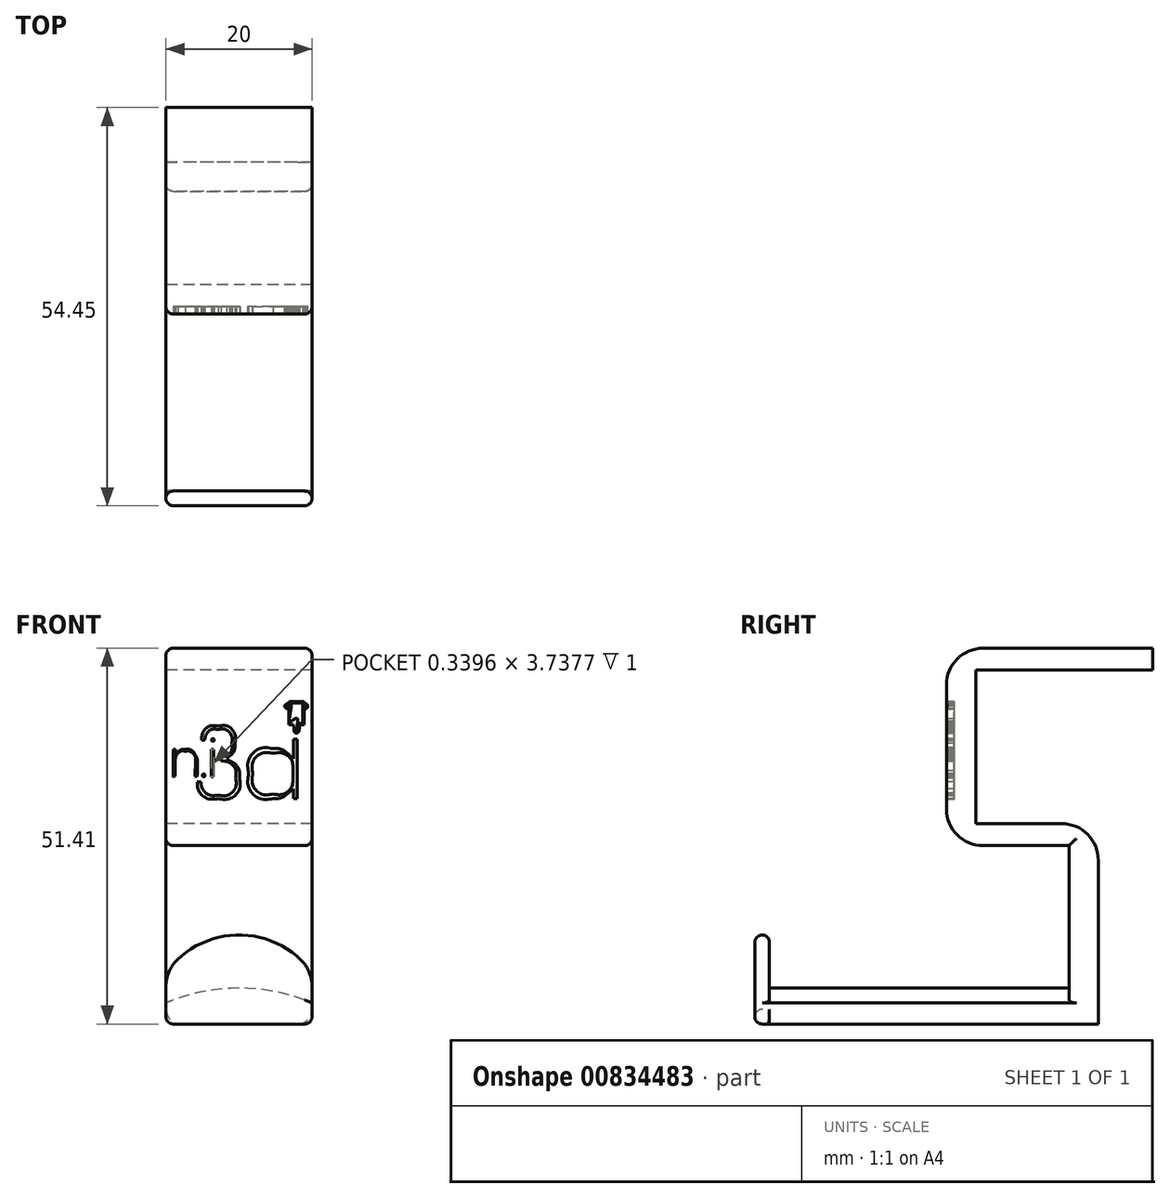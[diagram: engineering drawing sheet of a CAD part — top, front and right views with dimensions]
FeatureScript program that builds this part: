
annotation { "Feature Type Name" : "Feature", "Feature Type Description" : "" }
export const myFeature = defineFeature(function(context is Context, id is Id, definition is map)
    precondition{}
    {
        {
            var Q0;
            Q0=qCreatedBy(makeId("Right.planeOp"),FACE);
            var sketch = newSketch(context, id + "F0", { "sketchPlane" : qUnion([Q0])});
            skLineSegment(sketch, "E0", {"start": v(-10.53, 4.55) * mm, "end": v(13.69, 4.55) * mm});
            skLineSegment(sketch, "E1", {"start": v(13.69, 4.55) * mm, "end": v(13.69, 7.55) * mm});
            skLineSegment(sketch, "E2", {"start": v(13.69, 7.55) * mm, "end": v(-14.53, 7.55) * mm});
            skLineSegment(sketch, "E3", {"start": v(-14.53, 7.55) * mm, "end": v(-14.53, -19.45) * mm});
            skLineSegment(sketch, "E4", {"start": v(-14.53, -19.45) * mm, "end": v(2.24, -19.45) * mm});
            skLineSegment(sketch, "E5", {"start": v(2.24, -19.45) * mm, "end": v(2.24, -43.86) * mm});
            skLineSegment(sketch, "E6", {"start": v(2.24, -43.86) * mm, "end": v(6.24, -43.86) * mm});
            skLineSegment(sketch, "E7", {"start": v(6.24, -43.86) * mm, "end": v(6.24, -16.45) * mm});
            skLineSegment(sketch, "E8", {"start": v(6.24, -16.45) * mm, "end": v(-10.53, -16.45) * mm});
            skLineSegment(sketch, "E9", {"start": v(-10.53, -16.45) * mm, "end": v(-10.53, 4.55) * mm});
            skSolve(sketch);
        }
        {
            var Q0;
            Q0=makeQuery(id+"F0.imprint","IMPRINT",FACE,{"disambiguationData":[TD([[makeQuery(id+"F0.imprint","IMPRINT",EDGE,{"derivedFrom":sQuery(id+"F0.wireOp",EDGE,"E0")}),1.0]])]});
            extrude(context, id + "F1", {"entities" : qUnion([Q0]), "depth" : 20 * mm, "offsetDistance" : 25 * mm});
        }
        {
            var Q0;
            Q0=makeQuery(id+"F1.opExtrude","SWEPT_FACE",FACE,{"disambiguationData":[OSD([sQuery(id+"F0.wireOp",EDGE,"E7")])]});
            var sketch = newSketch(context, id + "F2", { "sketchPlane" : qUnion([Q0])});
            skLineSegment(sketch, "E10", {"start": v(-20, -43.86) * mm, "end": v(0, -43.86) * mm, "construction": true});
            skPoint(sketch, "E11", {"position": v(-10, -43.86) * mm});
            skArc(sketch, "E12", {"start": v(0, -40.98) * mm, "mid": v(-10, -38.94) * mm, "end": v(-20, -40.98) * mm});
            skLineSegment(sketch, "E13", {"start": v(0, -43.86) * mm, "end": v(-20, -43.86) * mm});
            skLineSegment(sketch, "E14", {"start": v(0, -40.98) * mm, "end": v(0, -43.86) * mm});
            skLineSegment(sketch, "E15", {"start": v(-20, -40.98) * mm, "end": v(-20, -43.86) * mm});
            skPoint(sketch, "E16.orphan", {"position": v(-25.08, -43.86) * mm});
            skPoint(sketch, "E17.orphan", {"position": v(5.08, -43.86) * mm});
            skSolve(sketch);
        }
        {
            var Q0;
            {var subQ0=sQuery(id+"F2.wireOp",EDGE,"E13");var subQ1=sQuery(id+"F2.wireOp",EDGE,"E12");var subQ2=makeQuery(id+"F2.imprint","INTERSECT",VERTEX,{"disambiguationData":[OD(1.0)],"derivedFrom":[subQ1,subQ0]});Q0=makeQuery(id+"F2.imprint","IMPRINT",FACE,{"disambiguationData":[TD([[makeQuery(id+"F2.imprint","IMPRINT",EDGE,{"disambiguationData":[TD([[subQ2,1.0]])],"derivedFrom":subQ1}),1.0]])]});}
            var Q1;
            {var subQ0=sQuery(id+"F2.wireOp",EDGE,"E13");var subQ1=sQuery(id+"F2.wireOp",EDGE,"E12");var subQ2=makeQuery(id+"F2.imprint","INTERSECT",VERTEX,{"disambiguationData":[OD(0.0)],"derivedFrom":[subQ1,subQ0]});Q1=makeQuery(id+"F2.imprint","IMPRINT",FACE,{"disambiguationData":[TD([[makeQuery(id+"F2.imprint","IMPRINT",EDGE,{"disambiguationData":[TD([[subQ2,-1.0]])],"derivedFrom":subQ1}),1.0]])]});}
            var Q2;
            {var subQ0=sQuery(id+"F2.wireOp",EDGE,"E12");var subQ1=sQuery(id+"F0.wireOp",EDGE,"E5");var subQ2=makeQuery(id+"F1.opExtrude","CAP_EDGE",EDGE,{"disambiguationData":[OSD([subQ1])],"isStart":false});var subQ3=makeQuery(id+"F2.imprint","INTERSECT",VERTEX,{"derivedFrom":[subQ2,subQ0]});Q2=makeQuery(id+"F2.imprint","IMPRINT",FACE,{"disambiguationData":[TD([[makeQuery(id+"F2.imprint","IMPRINT",EDGE,{"disambiguationData":[TD([[subQ3,-1.0]])],"derivedFrom":subQ0}),1.0]])]});}
            var Q3;
            {var subQ0=sQuery(id+"F2.wireOp",EDGE,"E12");var subQ1=sQuery(id+"F0.wireOp",EDGE,"E7");var subQ2=makeQuery(id+"F1.opExtrude","CAP_EDGE",EDGE,{"disambiguationData":[OSD([subQ1])],"isStart":true});var subQ3=makeQuery(id+"F2.imprint","INTERSECT",VERTEX,{"derivedFrom":[subQ2,subQ0]});Q3=makeQuery(id+"F2.imprint","IMPRINT",FACE,{"disambiguationData":[TD([[makeQuery(id+"F2.imprint","IMPRINT",EDGE,{"disambiguationData":[TD([[subQ3,-1.0]])],"derivedFrom":subQ0}),1.0]])]});}
            extrude(context, id + "F3", {"entities" : qUnion([Q0, Q1, Q2, Q3]), "operationType" : NewBodyOperationType.ADD, "oppositeDirection" : true, "depth" : 45 * mm, "offsetDistance" : 25 * mm});
        }
        {
            var Q0;
            {var subQ0=sQuery(id+"F2.wireOp",EDGE,"E13");var subQ1=sQuery(id+"F2.wireOp",EDGE,"E12");Q0=makeQuery(id+"F3.opExtrude","SWEPT_EDGE",EDGE,{"disambiguationData":[OSD([subQ1,subQ0]),TDD([makeQuery(id+"F2.imprint","INTERSECT",VERTEX,{"disambiguationData":[OD(0.0)],"derivedFrom":[subQ1,subQ0]})])]});}
            var Q1;
            {var subQ0=sQuery(id+"F2.wireOp",EDGE,"E13");var subQ1=sQuery(id+"F2.wireOp",EDGE,"E12");Q1=makeQuery(id+"F3.opExtrude","SWEPT_EDGE",EDGE,{"disambiguationData":[OSD([subQ1,subQ0]),TDD([makeQuery(id+"F2.imprint","INTERSECT",VERTEX,{"disambiguationData":[OD(1.0)],"derivedFrom":[subQ1,subQ0]})])]});}
            fillet(context, id + "F4", {"entities" : qUnion([Q0, Q1]), "tangentPropagation" : true, "radius" : 2 * mm, "defaultsChanged" : true, "vertexSettings" : [], "allowEdgeOverflow" : false});
        }
        {
            var Q0;
            Q0=makeQuery(id+"F1.opExtrude","SWEPT_EDGE",EDGE,{"disambiguationData":[OSD([sQuery(id+"F0.wireOp",EDGE,"E2"),sQuery(id+"F0.wireOp",EDGE,"E3")])]});
            var Q1;
            Q1=makeQuery(id+"F1.opExtrude","SWEPT_EDGE",EDGE,{"disambiguationData":[OSD([sQuery(id+"F0.wireOp",EDGE,"E3"),sQuery(id+"F0.wireOp",EDGE,"E4")])]});
            fillet(context, id + "F5", {"entities" : qUnion([Q0, Q1]), "tangentPropagation" : true, "radius" : 5 * mm, "defaultsChanged" : false, "vertexSettings" : [], "allowEdgeOverflow" : false});
        }
        {
            var Q0;
            Q0=makeQuery(id+"F1.opExtrude","SWEPT_EDGE",EDGE,{"disambiguationData":[OSD([sQuery(id+"F0.wireOp",EDGE,"E7"),sQuery(id+"F0.wireOp",EDGE,"E8")])]});
            fillet(context, id + "F6", {"entities" : qUnion([Q0]), "tangentPropagation" : true, "radius" : 5 * mm, "defaultsChanged" : false, "vertexSettings" : [], "allowEdgeOverflow" : false});
        }
        {
            var Q0;
            Q0=makeQuery(id+"F3.opExtrude","CAP_FACE",FACE,{"disambiguationData":[OSD([sQuery(id+"F2.wireOp",EDGE,"E12"),sQuery(id+"F2.wireOp",EDGE,"E13")])],"isStart":false});
            var sketch = newSketch(context, id + "F7", { "sketchPlane" : qUnion([Q0])});
            skArc(sketch, "E18", {"start": v(0, -36.9) * mm, "mid": v(10, -31.68) * mm, "end": v(20, -36.9) * mm});
            skPoint(sketch, "E18.startSnap0", {"position": v(10, -43.86) * mm});
            skLineSegment(sketch, "E19", {"start": v(0, -43.86) * mm, "end": v(20, -43.86) * mm});
            skLineSegment(sketch, "E20", {"start": v(20, -36.9) * mm, "end": v(20, -43.86) * mm});
            skLineSegment(sketch, "E21", {"start": v(0, -36.9) * mm, "end": v(0, -43.86) * mm});
            skSolve(sketch);
        }
        {
            var Q0;
            Q0 = qSketchRegion(id + "F7", true);
            extrude(context, id + "F8", {"entities" : qUnion([Q0]), "operationType" : NewBodyOperationType.ADD, "depth" : 2 * mm, "offsetDistance" : 25 * mm});
        }
        {
            var Q0;
            Q0=makeQuery(id+"F1.opExtrude","SWEPT_FACE",FACE,{"disambiguationData":[OSD([sQuery(id+"F0.wireOp",EDGE,"E3")])]});
            var sketch = newSketch(context, id + "F9", { "sketchPlane" : qUnion([Q0])});
            skLineSegment(sketch, "E22", {"start": v(4.02, -7.84) * mm, "end": v(4, -10) * mm});
            skLineSegment(sketch, "E23", {"start": v(4, -10) * mm, "end": v(4.27, -10) * mm});
            skLineSegment(sketch, "E24", {"start": v(1.3, -7.04) * mm, "end": v(1.3, -6.28) * mm});
            skLineSegment(sketch, "E25", {"start": v(1.3, -6.28) * mm, "end": v(1.02, -6.27) * mm});
            skLineSegment(sketch, "E26", {"start": v(1.02, -6.27) * mm, "end": v(0.98, -9.98) * mm});
            skLineSegment(sketch, "E27", {"start": v(0.98, -9.98) * mm, "end": v(1.26, -9.98) * mm});
            skLineSegment(sketch, "E28", {"start": v(1.26, -9.98) * mm, "end": v(1.28, -7.62) * mm});
            skLineSegment(sketch, "E29", {"start": v(6.24, -6.32) * mm, "end": v(6.2, -10.05) * mm});
            skLineSegment(sketch, "E30", {"start": v(6.2, -10.05) * mm, "end": v(6.5, -10.06) * mm});
            skLineSegment(sketch, "E31", {"start": v(6.5, -10.06) * mm, "end": v(6.54, -6.32) * mm});
            skLineSegment(sketch, "E32", {"start": v(6.54, -6.32) * mm, "end": v(6.24, -6.32) * mm});
            skLineSegment(sketch, "E33", {"start": v(8.78, -7.86) * mm, "end": v(8.34, -7.56) * mm});
            skLineSegment(sketch, "E34", {"start": v(8.34, -7.56) * mm, "end": v(8.72, -7.2) * mm});
            skLineSegment(sketch, "E35", {"start": v(4.88, -5.05) * mm, "end": v(5.33, -5.05) * mm});
            skLineSegment(sketch, "E36", {"start": v(7.56, -7.32) * mm, "end": v(7.56, -7.89) * mm});
            skLineSegment(sketch, "E37", {"start": v(4.8, -10.71) * mm, "end": v(4.27, -10.71) * mm});
            skLineSegment(sketch, "E38", {"start": v(16.72, -12.25) * mm, "end": v(17.43, -11.66) * mm});
            skLineSegment(sketch, "E39", {"start": v(17.43, -11.66) * mm, "end": v(17.43, -13.01) * mm});
            skLineSegment(sketch, "E40", {"start": v(17.43, -13.01) * mm, "end": v(17.98, -13.01) * mm});
            skLineSegment(sketch, "E41", {"start": v(17.98, -13.01) * mm, "end": v(17.98, -4.92) * mm});
            skLineSegment(sketch, "E42", {"start": v(17.98, -4.92) * mm, "end": v(17.43, -4.92) * mm});
            skLineSegment(sketch, "E43", {"start": v(17.43, -4.92) * mm, "end": v(17.43, -7.54) * mm});
            skLineSegment(sketch, "E44", {"start": v(17.43, -7.54) * mm, "end": v(16.72, -6.94) * mm});
            skLineSegment(sketch, "E45", {"start": v(17.38, -9.23) * mm, "end": v(17.38, -9.96) * mm});
            skLineSegment(sketch, "E46", {"start": v(17.5, -3.3) * mm, "end": v(17.47, -2.93) * mm});
            skLineSegment(sketch, "E47", {"start": v(17.47, -2.93) * mm, "end": v(17.16, -2.92) * mm});
            skLineSegment(sketch, "E48", {"start": v(17.16, -2.92) * mm, "end": v(16.84, -2.9) * mm});
            skLineSegment(sketch, "E49", {"start": v(16.84, -2.9) * mm, "end": v(16.83, -1.34) * mm});
            skLineSegment(sketch, "E50", {"start": v(16.83, -1.34) * mm, "end": v(16.82, 0.23) * mm});
            skLineSegment(sketch, "E51", {"start": v(16.82, 0.23) * mm, "end": v(17.88, 0.23) * mm});
            skLineSegment(sketch, "E52", {"start": v(17.88, 0.23) * mm, "end": v(18.94, 0.23) * mm});
            skLineSegment(sketch, "E53", {"start": v(18.94, 0.23) * mm, "end": v(18.93, -1.34) * mm});
            skLineSegment(sketch, "E54", {"start": v(18.93, -1.34) * mm, "end": v(18.92, -2.9) * mm});
            skLineSegment(sketch, "E55", {"start": v(18.92, -2.9) * mm, "end": v(18.6, -2.92) * mm});
            skLineSegment(sketch, "E56", {"start": v(18.6, -2.92) * mm, "end": v(18.3, -2.93) * mm});
            skLineSegment(sketch, "E57", {"start": v(18.3, -2.93) * mm, "end": v(18.27, -3.27) * mm});
            skLineSegment(sketch, "E58", {"start": v(18.08, -3.19) * mm, "end": v(18.1, -2.74) * mm});
            skLineSegment(sketch, "E59", {"start": v(18.1, -2.74) * mm, "end": v(18.43, -2.74) * mm});
            skLineSegment(sketch, "E60", {"start": v(18.43, -2.74) * mm, "end": v(18.75, -2.74) * mm});
            skLineSegment(sketch, "E61", {"start": v(18.75, -2.74) * mm, "end": v(18.75, -1.35) * mm});
            skLineSegment(sketch, "E62", {"start": v(18.75, -1.35) * mm, "end": v(18.75, 0.04) * mm});
            skLineSegment(sketch, "E63", {"start": v(18.75, 0.04) * mm, "end": v(18.33, 0.04) * mm});
            skLineSegment(sketch, "E64", {"start": v(18.33, 0.04) * mm, "end": v(17.91, 0.04) * mm});
            skLineSegment(sketch, "E65", {"start": v(17.91, 0.04) * mm, "end": v(17.05, 0.02) * mm});
            skFitSpline(sketch, "E66", {"points": [v(2.67, -6.55) * mm, v(3.3, -6.55) * mm, v(3.97, -7.17) * mm, v(4.02, -7.84) * mm]});
            skFitSpline(sketch, "E67", {"points": [v(4.27, -10) * mm, v(4.31, -8.36) * mm, v(4.3, -8.07) * mm, v(4.3, -7.94) * mm]});
            skFitSpline(sketch, "E68", {"points": [v(4.3, -7.94) * mm, v(4.28, -7.66) * mm, v(4.2, -7.38) * mm, v(4.06, -7.14) * mm]});
            skFitSpline(sketch, "E69", {"points": [v(4.06, -7.14) * mm, v(3.76, -6.6) * mm, v(3.24, -6.28) * mm, v(2.67, -6.28) * mm]});
            skFitSpline(sketch, "E70", {"points": [v(2.67, -6.28) * mm, v(2.31, -6.27) * mm, v(1.96, -6.4) * mm, v(1.67, -6.63) * mm]});
            skFitSpline(sketch, "E71", {"points": [v(1.67, -6.63) * mm, v(1.49, -6.77) * mm, v(1.3, -7.02) * mm, v(1.3, -7.04) * mm, v(1.3, -7.04) * mm, v(1.3, -7.04) * mm]});
            skFitSpline(sketch, "E72", {"points": [v(1.28, -7.62) * mm, v(1.47, -6.99) * mm, v(2.04, -6.54) * mm, v(2.67, -6.55) * mm]});
            skFitSpline(sketch, "E73", {"points": [v(5.18, -9.68) * mm, v(5.1, -9.68) * mm, v(5.02, -9.76) * mm, v(5.02, -9.85) * mm]});
            skFitSpline(sketch, "E74", {"points": [v(5.02, -9.85) * mm, v(5.02, -9.94) * mm, v(5.1, -10) * mm, v(5.18, -10.01) * mm]});
            skFitSpline(sketch, "E75", {"points": [v(5.18, -10.01) * mm, v(5.28, -10.01) * mm, v(5.34, -9.95) * mm, v(5.35, -9.85) * mm]});
            skFitSpline(sketch, "E76", {"points": [v(5.35, -9.85) * mm, v(5.35, -9.76) * mm, v(5.28, -9.68) * mm, v(5.18, -9.68) * mm]});
            skFitSpline(sketch, "E77", {"points": [v(6.42, -5.17) * mm, v(6.52, -5.18) * mm, v(6.6, -5.1) * mm, v(6.6, -5.01) * mm]});
            skFitSpline(sketch, "E78", {"points": [v(6.6, -5.01) * mm, v(6.6, -4.92) * mm, v(6.52, -4.84) * mm, v(6.43, -4.84) * mm]});
            skFitSpline(sketch, "E79", {"points": [v(6.43, -4.84) * mm, v(6.34, -4.84) * mm, v(6.26, -4.91) * mm, v(6.25, -5) * mm]});
            skFitSpline(sketch, "E80", {"points": [v(6.25, -5) * mm, v(6.25, -5.1) * mm, v(6.33, -5.17) * mm, v(6.42, -5.17) * mm]});
            skFitSpline(sketch, "E81", {"points": [v(7.14, -13.03) * mm, v(8.75, -13.03) * mm, v(10.06, -11.76) * mm, v(10.06, -10.2) * mm]});
            skFitSpline(sketch, "E82", {"points": [v(10.06, -10.2) * mm, v(10.06, -9.26) * mm, v(9.58, -8.4) * mm, v(8.78, -7.86) * mm]});
            skFitSpline(sketch, "E83", {"points": [v(8.72, -7.2) * mm, v(9.19, -6.75) * mm, v(9.44, -6.14) * mm, v(9.44, -5.48) * mm]});
            skFitSpline(sketch, "E84", {"points": [v(9.44, -5.48) * mm, v(9.44, -4.16) * mm, v(8.4, -3.1) * mm, v(7.14, -3.1) * mm]});
            skFitSpline(sketch, "E85", {"points": [v(7.14, -3.1) * mm, v(6, -3.1) * mm, v(5.06, -3.95) * mm, v(4.88, -5.05) * mm]});
            skFitSpline(sketch, "E86", {"points": [v(5.33, -5.05) * mm, v(5.52, -4.2) * mm, v(6.26, -3.57) * mm, v(7.14, -3.57) * mm]});
            skFitSpline(sketch, "E87", {"points": [v(7.14, -3.57) * mm, v(8.17, -3.57) * mm, v(9, -4.43) * mm, v(9, -5.48) * mm]});
            skFitSpline(sketch, "E88", {"points": [v(9, -5.48) * mm, v(9, -6.38) * mm, v(8.4, -7.13) * mm, v(7.56, -7.32) * mm]});
            skFitSpline(sketch, "E89", {"points": [v(7.56, -7.89) * mm, v(8.7, -8.09) * mm, v(9.54, -9.05) * mm, v(9.54, -10.2) * mm]});
            skFitSpline(sketch, "E90", {"points": [v(9.54, -10.2) * mm, v(9.54, -11.49) * mm, v(8.47, -12.55) * mm, v(7.14, -12.55) * mm]});
            skFitSpline(sketch, "E91", {"points": [v(7.14, -12.55) * mm, v(6, -12.55) * mm, v(5.04, -11.77) * mm, v(4.8, -10.71) * mm]});
            skFitSpline(sketch, "E92", {"points": [v(4.27, -10.71) * mm, v(4.53, -12.03) * mm, v(5.73, -13.03) * mm, v(7.14, -13.03) * mm]});
            skFitSpline(sketch, "E93", {"points": [v(14.63, -6.18) * mm, v(12.81, -6.18) * mm, v(11.31, -7.72) * mm, v(11.31, -9.6) * mm]});
            skFitSpline(sketch, "E94", {"points": [v(11.31, -9.6) * mm, v(11.31, -11.47) * mm, v(12.81, -13.01) * mm, v(14.63, -13.01) * mm]});
            skFitSpline(sketch, "E95", {"points": [v(14.63, -13.01) * mm, v(15.4, -13.01) * mm, v(16.11, -12.75) * mm, v(16.72, -12.25) * mm]});
            skFitSpline(sketch, "E96", {"points": [v(16.72, -6.94) * mm, v(16.11, -6.45) * mm, v(15.4, -6.18) * mm, v(14.63, -6.18) * mm]});
            skFitSpline(sketch, "E97", {"points": [v(14.63, -12.4) * mm, v(13.08, -12.4) * mm, v(11.9, -11.18) * mm, v(11.9, -9.6) * mm]});
            skFitSpline(sketch, "E98", {"points": [v(11.9, -9.6) * mm, v(11.9, -8.02) * mm, v(13.08, -6.83) * mm, v(14.63, -6.83) * mm]});
            skFitSpline(sketch, "E99", {"points": [v(14.63, -6.83) * mm, v(16.04, -6.83) * mm, v(17.2, -7.8) * mm, v(17.38, -9.23) * mm]});
            skFitSpline(sketch, "E100", {"points": [v(17.38, -9.96) * mm, v(17.2, -11.4) * mm, v(16.04, -12.4) * mm, v(14.63, -12.4) * mm]});
            skFitSpline(sketch, "E101", {"points": [v(17.7, -4.01) * mm, v(17.58, -3.89) * mm, v(17.52, -3.68) * mm, v(17.5, -3.3) * mm]});
            skFitSpline(sketch, "E102", {"points": [v(18.27, -3.27) * mm, v(18.24, -3.68) * mm, v(18.2, -3.83) * mm, v(18.05, -4.02) * mm]});
            skFitSpline(sketch, "E103", {"points": [v(18.05, -4.02) * mm, v(17.98, -4.04) * mm, v(17.78, -4.06) * mm, v(17.7, -4.01) * mm]});
            skFitSpline(sketch, "E104", {"points": [v(18, -3.77) * mm, v(18.03, -3.69) * mm, v(18.06, -3.47) * mm, v(18.08, -3.19) * mm]});
            skFitSpline(sketch, "E105", {"points": [v(17.05, 0.02) * mm, v(17.13, -0.43) * mm, v(16.92, -2.55) * mm, v(17.24, -2.41) * mm]});
            skFitSpline(sketch, "E106", {"points": [v(17.24, -2.41) * mm, v(17.98, -2.09) * mm, v(17.86, -3.93) * mm, v(17.9, -3.91) * mm]});
            skFitSpline(sketch, "E107", {"points": [v(17.9, -3.91) * mm, v(17.91, -3.9) * mm, v(17.96, -3.84) * mm, v(18, -3.77) * mm]});
            skFitSpline(sketch, "E108", {"points": [v(16.42, -0.63) * mm, v(16.29, -0.5) * mm, v(16.28, -0.27) * mm, v(16.42, -0.14) * mm]});
            skFitSpline(sketch, "E109", {"points": [v(16.42, -0.14) * mm, v(16.47, -0.08) * mm, v(16.55, -0.04) * mm, v(16.6, -0.04) * mm]});
            skFitSpline(sketch, "E110", {"points": [v(16.6, -0.04) * mm, v(16.66, -0.04) * mm, v(16.67, -0.07) * mm, v(16.67, -0.39) * mm]});
            skFitSpline(sketch, "E111", {"points": [v(16.67, -0.39) * mm, v(16.67, -0.7) * mm, v(16.66, -0.73) * mm, v(16.6, -0.73) * mm]});
            skFitSpline(sketch, "E112", {"points": [v(16.6, -0.73) * mm, v(16.56, -0.73) * mm, v(16.48, -0.69) * mm, v(16.42, -0.63) * mm]});
            skFitSpline(sketch, "E113", {"points": [v(19.02, -0.39) * mm, v(19.02, -0.08) * mm, v(19.02, -0.04) * mm, v(19.09, -0.04) * mm]});
            skFitSpline(sketch, "E114", {"points": [v(19.09, -0.04) * mm, v(19.2, -0.04) * mm, v(19.35, -0.18) * mm, v(19.37, -0.3) * mm]});
            skFitSpline(sketch, "E115", {"points": [v(19.37, -0.3) * mm, v(19.4, -0.44) * mm, v(19.34, -0.6) * mm, v(19.23, -0.67) * mm]});
            skFitSpline(sketch, "E116", {"points": [v(19.23, -0.67) * mm, v(19.04, -0.8) * mm, v(19.02, -0.77) * mm, v(19.02, -0.39) * mm]});
            skFitSpline(sketch, "E117", {"points": [v(17.3, -5.04) * mm, v(17.15, -4.77) * mm, v(17.22, -4.57) * mm, v(17.52, -4.33) * mm]});
            skFitSpline(sketch, "E118", {"points": [v(17.52, -4.33) * mm, v(17.75, -4.14) * mm, v(17.8, -4.07) * mm, v(17.73, -4) * mm]});
            skFitSpline(sketch, "E119", {"points": [v(17.73, -4) * mm, v(17.98, -4) * mm, v(18.01, -4) * mm, v(18.02, -4) * mm, v(18.02, -4) * mm, v(18.02, -4) * mm]});
            skFitSpline(sketch, "E120", {"points": [v(18.02, -4) * mm, v(17.97, -4.07) * mm, v(17.93, -4.15) * mm, v(17.93, -4.17) * mm]});
            skFitSpline(sketch, "E121", {"points": [v(17.93, -4.17) * mm, v(17.93, -4.19) * mm, v(17.86, -4.26) * mm, v(17.78, -4.34) * mm]});
            skFitSpline(sketch, "E122", {"points": [v(17.78, -4.34) * mm, v(17.38, -4.72) * mm, v(17.4, -4.7) * mm, v(17.41, -4.83) * mm]});
            skFitSpline(sketch, "E123", {"points": [v(17.41, -4.83) * mm, v(17.45, -4.9) * mm, v(17.35, -5.1) * mm, v(17.3, -5.04) * mm]});
            skSolve(sketch);
        }
        {
            var Q0;
            Q0 = qSketchRegion(id + "F9", true);
            extrude(context, id + "F10", {"entities" : qUnion([Q0]), "operationType" : NewBodyOperationType.REMOVE, "oppositeDirection" : true, "depth" : 1 * mm, "offsetDistance" : 25 * mm});
        }
        {
            var Q0;
            Q0=makeQuery(id+"F8.opExtrude","SWEPT_EDGE",EDGE,{"disambiguationData":[OSD([sQuery(id+"F7.wireOp",EDGE,"E19"),sQuery(id+"F7.wireOp",EDGE,"E20")])]});
            var Q1;
            Q1=makeQuery(id+"F8.opExtrude","SWEPT_EDGE",EDGE,{"disambiguationData":[OSD([sQuery(id+"F7.wireOp",EDGE,"E19"),sQuery(id+"F7.wireOp",EDGE,"E21")])]});
            fillet(context, id + "F11", {"entities" : qUnion([Q0, Q1]), "tangentPropagation" : true, "radius" : 1 * mm, "defaultsChanged" : true, "vertexSettings" : [], "allowEdgeOverflow" : false});
        }
        {
            var Q0;
            Q0=makeQuery(id+"F8.opExtrude","SWEPT_EDGE",EDGE,{"disambiguationData":[OSD([sQuery(id+"F7.wireOp",EDGE,"E18"),sQuery(id+"F7.wireOp",EDGE,"E21")])]});
            var Q1;
            Q1=makeQuery(id+"F8.opExtrude","SWEPT_EDGE",EDGE,{"disambiguationData":[OSD([sQuery(id+"F7.wireOp",EDGE,"E18"),sQuery(id+"F7.wireOp",EDGE,"E20")])]});
            fillet(context, id + "F12", {"entities" : qUnion([Q0, Q1]), "tangentPropagation" : true, "radius" : 5 * mm, "defaultsChanged" : false, "vertexSettings" : [], "allowEdgeOverflow" : false});
        }
        {
            var Q0;
            Q0=makeQuery(id+"F8.opExtrude","CAP_EDGE",EDGE,{"disambiguationData":[OSD([sQuery(id+"F7.wireOp",EDGE,"E18")])],"isStart":true});
            var Q1;
            Q1=makeQuery(id+"F8.opExtrude","CAP_EDGE",EDGE,{"disambiguationData":[OSD([sQuery(id+"F7.wireOp",EDGE,"E18")])],"isStart":false});
            var Q2;
            {var subQ0=sQuery(id+"F7.wireOp",EDGE,"E21");var subQ1=sQuery(id+"F7.wireOp",EDGE,"E18");Q2=makeQuery(id+"F12.opFillet","BLEND_EDGE",EDGE,{"blendedFrom":[makeQuery(id+"F8.opExtrude","SWEPT_EDGE",EDGE,{"disambiguationData":[OSD([subQ1,subQ0])]}),makeQuery(id+"F8.opExtrude","CAP_FACE",FACE,{"disambiguationData":[OSD([subQ1,sQuery(id+"F7.wireOp",EDGE,"E19"),sQuery(id+"F7.wireOp",EDGE,"E20"),subQ0])],"isStart":false})],"blendedInto":[makeQuery(id+"F8.opExtrude","CAP_FACE",FACE,{"disambiguationData":[OSD([subQ1,sQuery(id+"F7.wireOp",EDGE,"E19"),sQuery(id+"F7.wireOp",EDGE,"E20"),subQ0])],"isStart":false})]});}
            var Q3;
            {var subQ0=sQuery(id+"F7.wireOp",EDGE,"E21");var subQ11=sQuery(id+"F7.wireOp",EDGE,"E18");var subQ12=sQuery(id+"F7.wireOp",EDGE,"E20");Q3=makeQuery(id+"F12.opFillet","BLEND_EDGE",EDGE,{"blendedFrom":[makeQuery(id+"F8.opExtrude","SWEPT_EDGE",EDGE,{"disambiguationData":[OSD([subQ11,subQ0])]}),makeQuery(id+"F8.boolean.opBoolean","SPLIT",FACE,{"disambiguationData":[TD([makeQuery(id+"F3.opExtrude","SWEPT_FACE",FACE,{"disambiguationData":[OSD([sQuery(id+"F2.wireOp",EDGE,"E12")])]})])],"derivedFrom":makeQuery(id+"F8.opExtrude","CAP_FACE",FACE,{"disambiguationData":[OSD([subQ11,sQuery(id+"F7.wireOp",EDGE,"E19"),subQ12,subQ0])],"isStart":true})})],"blendedInto":[makeQuery(id+"F8.boolean.opBoolean","SPLIT",FACE,{"disambiguationData":[TD([makeQuery(id+"F3.opExtrude","SWEPT_FACE",FACE,{"disambiguationData":[OSD([sQuery(id+"F2.wireOp",EDGE,"E12")])]})])],"derivedFrom":makeQuery(id+"F8.opExtrude","CAP_FACE",FACE,{"disambiguationData":[OSD([subQ11,sQuery(id+"F7.wireOp",EDGE,"E19"),subQ12,subQ0])],"isStart":true})})]});}
            var Q4;
            {var subQ0=sQuery(id+"F7.wireOp",EDGE,"E21");Q4=makeQuery(id+"F8.boolean.opBoolean","SPLIT",EDGE,{"disambiguationData":[TD([makeQuery(id+"F3.opExtrude","SWEPT_FACE",FACE,{"disambiguationData":[OSD([sQuery(id+"F2.wireOp",EDGE,"E12")])]})])],"derivedFrom":makeQuery(id+"F8.opExtrude","CAP_EDGE",EDGE,{"disambiguationData":[OSD([subQ0])],"isStart":true})});}
            var Q5;
            Q5=makeQuery(id+"F8.opExtrude","CAP_EDGE",EDGE,{"disambiguationData":[OSD([sQuery(id+"F7.wireOp",EDGE,"E21")])],"isStart":false});
            var Q6;
            {var subQ0=sQuery(id+"F7.wireOp",EDGE,"E20");var subQ1=sQuery(id+"F7.wireOp",EDGE,"E18");Q6=makeQuery(id+"F12.opFillet","BLEND_EDGE",EDGE,{"blendedFrom":[makeQuery(id+"F8.opExtrude","SWEPT_EDGE",EDGE,{"disambiguationData":[OSD([subQ1,subQ0])]}),makeQuery(id+"F8.opExtrude","CAP_FACE",FACE,{"disambiguationData":[OSD([subQ1,sQuery(id+"F7.wireOp",EDGE,"E19"),subQ0,sQuery(id+"F7.wireOp",EDGE,"E21")])],"isStart":false})],"blendedInto":[makeQuery(id+"F8.opExtrude","CAP_FACE",FACE,{"disambiguationData":[OSD([subQ1,sQuery(id+"F7.wireOp",EDGE,"E19"),subQ0,sQuery(id+"F7.wireOp",EDGE,"E21")])],"isStart":false})]});}
            var Q7;
            Q7=makeQuery(id+"F8.opExtrude","CAP_EDGE",EDGE,{"disambiguationData":[OSD([sQuery(id+"F7.wireOp",EDGE,"E20")])],"isStart":false});
            var Q8;
            {var subQ0=sQuery(id+"F7.wireOp",EDGE,"E21");var subQ1=sQuery(id+"F7.wireOp",EDGE,"E19");Q8=makeQuery(id+"F11.opFillet","BLEND_EDGE",EDGE,{"blendedFrom":[makeQuery(id+"F8.opExtrude","SWEPT_EDGE",EDGE,{"disambiguationData":[OSD([subQ1,subQ0])]}),makeQuery(id+"F8.opExtrude","CAP_FACE",FACE,{"disambiguationData":[OSD([sQuery(id+"F7.wireOp",EDGE,"E18"),subQ1,sQuery(id+"F7.wireOp",EDGE,"E20"),subQ0])],"isStart":false})],"blendedInto":[makeQuery(id+"F8.opExtrude","CAP_FACE",FACE,{"disambiguationData":[OSD([sQuery(id+"F7.wireOp",EDGE,"E18"),subQ1,sQuery(id+"F7.wireOp",EDGE,"E20"),subQ0])],"isStart":false})]});}
            var Q9;
            Q9=makeQuery(id+"F8.opExtrude","CAP_EDGE",EDGE,{"disambiguationData":[OSD([sQuery(id+"F7.wireOp",EDGE,"E19")])],"isStart":false});
            var Q10;
            {var subQ0=sQuery(id+"F7.wireOp",EDGE,"E20");var subQ1=sQuery(id+"F7.wireOp",EDGE,"E19");Q10=makeQuery(id+"F11.opFillet","BLEND_EDGE",EDGE,{"blendedFrom":[makeQuery(id+"F8.opExtrude","SWEPT_EDGE",EDGE,{"disambiguationData":[OSD([subQ1,subQ0])]}),makeQuery(id+"F8.opExtrude","CAP_FACE",FACE,{"disambiguationData":[OSD([sQuery(id+"F7.wireOp",EDGE,"E18"),subQ1,subQ0,sQuery(id+"F7.wireOp",EDGE,"E21")])],"isStart":false})],"blendedInto":[makeQuery(id+"F8.opExtrude","CAP_FACE",FACE,{"disambiguationData":[OSD([sQuery(id+"F7.wireOp",EDGE,"E18"),subQ1,subQ0,sQuery(id+"F7.wireOp",EDGE,"E21")])],"isStart":false})]});}
            var Q11;
            {var subQ0=sQuery(id+"F7.wireOp",EDGE,"E21");var subQ11=sQuery(id+"F7.wireOp",EDGE,"E18");var subQ12=sQuery(id+"F7.wireOp",EDGE,"E20");Q11=makeQuery(id+"F12.opFillet","BLEND_EDGE",EDGE,{"blendedFrom":[makeQuery(id+"F8.opExtrude","SWEPT_EDGE",EDGE,{"disambiguationData":[OSD([subQ11,subQ12])]}),makeQuery(id+"F8.boolean.opBoolean","SPLIT",FACE,{"disambiguationData":[TD([makeQuery(id+"F3.opExtrude","SWEPT_FACE",FACE,{"disambiguationData":[OSD([sQuery(id+"F2.wireOp",EDGE,"E12")])]})])],"derivedFrom":makeQuery(id+"F8.opExtrude","CAP_FACE",FACE,{"disambiguationData":[OSD([subQ11,sQuery(id+"F7.wireOp",EDGE,"E19"),subQ12,subQ0])],"isStart":true})})],"blendedInto":[makeQuery(id+"F8.boolean.opBoolean","SPLIT",FACE,{"disambiguationData":[TD([makeQuery(id+"F3.opExtrude","SWEPT_FACE",FACE,{"disambiguationData":[OSD([sQuery(id+"F2.wireOp",EDGE,"E12")])]})])],"derivedFrom":makeQuery(id+"F8.opExtrude","CAP_FACE",FACE,{"disambiguationData":[OSD([subQ11,sQuery(id+"F7.wireOp",EDGE,"E19"),subQ12,subQ0])],"isStart":true})})]});}
            var Q12;
            {var subQ1=sQuery(id+"F7.wireOp",EDGE,"E20");Q12=makeQuery(id+"F8.boolean.opBoolean","SPLIT",EDGE,{"disambiguationData":[TD([makeQuery(id+"F3.opExtrude","SWEPT_FACE",FACE,{"disambiguationData":[OSD([sQuery(id+"F2.wireOp",EDGE,"E12")])]})])],"derivedFrom":makeQuery(id+"F8.opExtrude","CAP_EDGE",EDGE,{"disambiguationData":[OSD([subQ1])],"isStart":true})});}
            fillet(context, id + "F13", {"entities" : qUnion([Q0, Q1, Q2, Q3, Q4, Q5, Q6, Q7, Q8, Q9, Q10, Q11, Q12]), "tangentPropagation" : true, "radius" : 1 * mm, "defaultsChanged" : true, "vertexSettings" : [], "allowEdgeOverflow" : false});
        }
        {
            var Q0;
            Q0=makeQuery(id+"F1.opExtrude","CAP_EDGE",EDGE,{"disambiguationData":[OSD([sQuery(id+"F0.wireOp",EDGE,"E3")])],"isStart":true});
            var Q1;
            {var subQ0=sQuery(id+"F0.wireOp",EDGE,"E3");var subQ1=sQuery(id+"F0.wireOp",EDGE,"E2");Q1=makeQuery(id+"F5.opFillet","BLEND_EDGE",EDGE,{"blendedFrom":[makeQuery(id+"F1.opExtrude","SWEPT_EDGE",EDGE,{"disambiguationData":[OSD([subQ1,subQ0])]}),makeQuery(id+"F3.boolean.opBoolean","MERGE",FACE,{"derivedFrom":[makeQuery(id+"F1.opExtrude","CAP_FACE",FACE,{"disambiguationData":[OSD([sQuery(id+"F0.wireOp",EDGE,"E0"),sQuery(id+"F0.wireOp",EDGE,"E1"),subQ1,subQ0,sQuery(id+"F0.wireOp",EDGE,"E4"),sQuery(id+"F0.wireOp",EDGE,"E5"),sQuery(id+"F0.wireOp",EDGE,"E6"),sQuery(id+"F0.wireOp",EDGE,"E7"),sQuery(id+"F0.wireOp",EDGE,"E8"),sQuery(id+"F0.wireOp",EDGE,"E9")])],"isStart":true}),makeQuery(id+"F3.opExtrude","SWEPT_FACE",FACE,{"disambiguationData":[OSD([sQuery(id+"F2.wireOp",EDGE,"E14")])]})]})],"blendedInto":[makeQuery(id+"F3.boolean.opBoolean","MERGE",FACE,{"derivedFrom":[makeQuery(id+"F1.opExtrude","CAP_FACE",FACE,{"disambiguationData":[OSD([sQuery(id+"F0.wireOp",EDGE,"E0"),sQuery(id+"F0.wireOp",EDGE,"E1"),subQ1,subQ0,sQuery(id+"F0.wireOp",EDGE,"E4"),sQuery(id+"F0.wireOp",EDGE,"E5"),sQuery(id+"F0.wireOp",EDGE,"E6"),sQuery(id+"F0.wireOp",EDGE,"E7"),sQuery(id+"F0.wireOp",EDGE,"E8"),sQuery(id+"F0.wireOp",EDGE,"E9")])],"isStart":true}),makeQuery(id+"F3.opExtrude","SWEPT_FACE",FACE,{"disambiguationData":[OSD([sQuery(id+"F2.wireOp",EDGE,"E14")])]})]})]});}
            var Q2;
            Q2=makeQuery(id+"F1.opExtrude","CAP_EDGE",EDGE,{"disambiguationData":[OSD([sQuery(id+"F0.wireOp",EDGE,"E2")])],"isStart":true});
            var Q3;
            Q3=makeQuery(id+"F1.opExtrude","CAP_EDGE",EDGE,{"disambiguationData":[OSD([sQuery(id+"F0.wireOp",EDGE,"E2")])],"isStart":false});
            var Q4;
            {var subQ0=sQuery(id+"F0.wireOp",EDGE,"E3");var subQ1=sQuery(id+"F0.wireOp",EDGE,"E2");Q4=makeQuery(id+"F5.opFillet","BLEND_EDGE",EDGE,{"blendedFrom":[makeQuery(id+"F1.opExtrude","SWEPT_EDGE",EDGE,{"disambiguationData":[OSD([subQ1,subQ0])]}),makeQuery(id+"F3.boolean.opBoolean","MERGE",FACE,{"derivedFrom":[makeQuery(id+"F1.opExtrude","CAP_FACE",FACE,{"disambiguationData":[OSD([sQuery(id+"F0.wireOp",EDGE,"E0"),sQuery(id+"F0.wireOp",EDGE,"E1"),subQ1,subQ0,sQuery(id+"F0.wireOp",EDGE,"E4"),sQuery(id+"F0.wireOp",EDGE,"E5"),sQuery(id+"F0.wireOp",EDGE,"E6"),sQuery(id+"F0.wireOp",EDGE,"E7"),sQuery(id+"F0.wireOp",EDGE,"E8"),sQuery(id+"F0.wireOp",EDGE,"E9")])],"isStart":false}),makeQuery(id+"F3.opExtrude","SWEPT_FACE",FACE,{"disambiguationData":[OSD([sQuery(id+"F2.wireOp",EDGE,"E15")])]})]})],"blendedInto":[makeQuery(id+"F3.boolean.opBoolean","MERGE",FACE,{"derivedFrom":[makeQuery(id+"F1.opExtrude","CAP_FACE",FACE,{"disambiguationData":[OSD([sQuery(id+"F0.wireOp",EDGE,"E0"),sQuery(id+"F0.wireOp",EDGE,"E1"),subQ1,subQ0,sQuery(id+"F0.wireOp",EDGE,"E4"),sQuery(id+"F0.wireOp",EDGE,"E5"),sQuery(id+"F0.wireOp",EDGE,"E6"),sQuery(id+"F0.wireOp",EDGE,"E7"),sQuery(id+"F0.wireOp",EDGE,"E8"),sQuery(id+"F0.wireOp",EDGE,"E9")])],"isStart":false}),makeQuery(id+"F3.opExtrude","SWEPT_FACE",FACE,{"disambiguationData":[OSD([sQuery(id+"F2.wireOp",EDGE,"E15")])]})]})]});}
            var Q5;
            Q5=makeQuery(id+"F1.opExtrude","CAP_EDGE",EDGE,{"disambiguationData":[OSD([sQuery(id+"F0.wireOp",EDGE,"E3")])],"isStart":false});
            var Q6;
            {var subQ0=sQuery(id+"F0.wireOp",EDGE,"E4");var subQ1=sQuery(id+"F0.wireOp",EDGE,"E3");Q6=makeQuery(id+"F5.opFillet","BLEND_EDGE",EDGE,{"blendedFrom":[makeQuery(id+"F1.opExtrude","SWEPT_EDGE",EDGE,{"disambiguationData":[OSD([subQ1,subQ0])]}),makeQuery(id+"F3.boolean.opBoolean","MERGE",FACE,{"derivedFrom":[makeQuery(id+"F1.opExtrude","CAP_FACE",FACE,{"disambiguationData":[OSD([sQuery(id+"F0.wireOp",EDGE,"E0"),sQuery(id+"F0.wireOp",EDGE,"E1"),sQuery(id+"F0.wireOp",EDGE,"E2"),subQ1,subQ0,sQuery(id+"F0.wireOp",EDGE,"E5"),sQuery(id+"F0.wireOp",EDGE,"E6"),sQuery(id+"F0.wireOp",EDGE,"E7"),sQuery(id+"F0.wireOp",EDGE,"E8"),sQuery(id+"F0.wireOp",EDGE,"E9")])],"isStart":false}),makeQuery(id+"F3.opExtrude","SWEPT_FACE",FACE,{"disambiguationData":[OSD([sQuery(id+"F2.wireOp",EDGE,"E15")])]})]})],"blendedInto":[makeQuery(id+"F3.boolean.opBoolean","MERGE",FACE,{"derivedFrom":[makeQuery(id+"F1.opExtrude","CAP_FACE",FACE,{"disambiguationData":[OSD([sQuery(id+"F0.wireOp",EDGE,"E0"),sQuery(id+"F0.wireOp",EDGE,"E1"),sQuery(id+"F0.wireOp",EDGE,"E2"),subQ1,subQ0,sQuery(id+"F0.wireOp",EDGE,"E5"),sQuery(id+"F0.wireOp",EDGE,"E6"),sQuery(id+"F0.wireOp",EDGE,"E7"),sQuery(id+"F0.wireOp",EDGE,"E8"),sQuery(id+"F0.wireOp",EDGE,"E9")])],"isStart":false}),makeQuery(id+"F3.opExtrude","SWEPT_FACE",FACE,{"disambiguationData":[OSD([sQuery(id+"F2.wireOp",EDGE,"E15")])]})]})]});}
            var Q7;
            Q7=makeQuery(id+"F1.opExtrude","CAP_EDGE",EDGE,{"disambiguationData":[OSD([sQuery(id+"F0.wireOp",EDGE,"E4")])],"isStart":false});
            var Q8;
            {var subQ0=sQuery(id+"F0.wireOp",EDGE,"E4");var subQ1=sQuery(id+"F0.wireOp",EDGE,"E3");Q8=makeQuery(id+"F5.opFillet","BLEND_EDGE",EDGE,{"blendedFrom":[makeQuery(id+"F1.opExtrude","SWEPT_EDGE",EDGE,{"disambiguationData":[OSD([subQ1,subQ0])]}),makeQuery(id+"F3.boolean.opBoolean","MERGE",FACE,{"derivedFrom":[makeQuery(id+"F1.opExtrude","CAP_FACE",FACE,{"disambiguationData":[OSD([sQuery(id+"F0.wireOp",EDGE,"E0"),sQuery(id+"F0.wireOp",EDGE,"E1"),sQuery(id+"F0.wireOp",EDGE,"E2"),subQ1,subQ0,sQuery(id+"F0.wireOp",EDGE,"E5"),sQuery(id+"F0.wireOp",EDGE,"E6"),sQuery(id+"F0.wireOp",EDGE,"E7"),sQuery(id+"F0.wireOp",EDGE,"E8"),sQuery(id+"F0.wireOp",EDGE,"E9")])],"isStart":true}),makeQuery(id+"F3.opExtrude","SWEPT_FACE",FACE,{"disambiguationData":[OSD([sQuery(id+"F2.wireOp",EDGE,"E14")])]})]})],"blendedInto":[makeQuery(id+"F3.boolean.opBoolean","MERGE",FACE,{"derivedFrom":[makeQuery(id+"F1.opExtrude","CAP_FACE",FACE,{"disambiguationData":[OSD([sQuery(id+"F0.wireOp",EDGE,"E0"),sQuery(id+"F0.wireOp",EDGE,"E1"),sQuery(id+"F0.wireOp",EDGE,"E2"),subQ1,subQ0,sQuery(id+"F0.wireOp",EDGE,"E5"),sQuery(id+"F0.wireOp",EDGE,"E6"),sQuery(id+"F0.wireOp",EDGE,"E7"),sQuery(id+"F0.wireOp",EDGE,"E8"),sQuery(id+"F0.wireOp",EDGE,"E9")])],"isStart":true}),makeQuery(id+"F3.opExtrude","SWEPT_FACE",FACE,{"disambiguationData":[OSD([sQuery(id+"F2.wireOp",EDGE,"E14")])]})]})]});}
            var Q9;
            Q9=makeQuery(id+"F1.opExtrude","CAP_EDGE",EDGE,{"disambiguationData":[OSD([sQuery(id+"F0.wireOp",EDGE,"E4")])],"isStart":true});
            var Q10;
            Q10=makeQuery(id+"F1.opExtrude","CAP_EDGE",EDGE,{"disambiguationData":[OSD([sQuery(id+"F0.wireOp",EDGE,"E5")])],"isStart":true});
            var Q11;
            Q11=makeQuery(id+"F1.opExtrude","CAP_EDGE",EDGE,{"disambiguationData":[OSD([sQuery(id+"F0.wireOp",EDGE,"E5")])],"isStart":false});
            fillet(context, id + "F14", {"entities" : qUnion([Q0, Q1, Q2, Q3, Q4, Q5, Q6, Q7, Q8, Q9, Q10, Q11]), "tangentPropagation" : true, "radius" : 1 * mm, "defaultsChanged" : false, "vertexSettings" : [], "allowEdgeOverflow" : false});
        }
    });
